# Revit family: Spout_Wall_Abey_Vela_165_FaceBased
name_source: partatom
category: Plumbing Fixtures
units: mm (PartAtom-declared; Revit-internal decimal feet)

## family parameters
Cut with Voids When Loaded = No
Host = Face
OmniClass Number = 23.31.11.00
OmniClass Title = Faucets
Part Type = Normal
Room Calculation Point = No
Round Connector Dimension = Use Diameter
Shared = No

## types (5) — shared parameters
Assembly Code = C1030210
CW Connection = Yes
Default Elevation = 0 mm
Description = Manufactured from low-lead brass, the Vela Bathroom Collection will transform your bathroom into a sanctuary of grace, serenity and purification.
HW Connection = Yes
IfcExportAs = ifcValve
IfcExportType = FAUCET
Manufacturer = Abey
ManufacturerOverallDepth = 182 mm
ManufacturerOverallHeight = 65 mm
ManufacturerOverallWidth = 65 mm
ManufacturerURLProductSpecific = https://www.abey.com.au
ModifiedIssue = 20230628 $
URL = https://www.abey.com.au
Uniclass2015Code = Pr_40_20_87_97
Uniclass2015Title = Washbasin spouts
Uniclass2015Version = Products v1.28
Vent Connection = No
Waste Connection = No
zero-valued in all types: Cost

## per-type parameters (varying)
| type | BodyMaterial | ManufacturerSpecCode | Model | Type Comments |
| Black (7S-C165-B) | Metal_Abey_Black | 7S-C165-B | 7S-C165-B | Black |
| Brushed Brass (7S-C165-BB) | Metal_Abey_Brass | 7S-C165-BB | 7S-C165-BB | Brushed Brass |
| Brushed Nickel (7S-C165-BN) | Metal_Abey_BrushedNickel | 7S-C165-BN | 7S-C165-BN | Brushed Nickel |
| Chrome (7S-C165) | Metal_Abey_Chrome | 7S-C165 | 7S-C165 | Chrome |
| Gun Metal (7S-C165-GM) | Metal_Abey_GunMetal | 7S-C165-GM | 7S-C165-GM | Gun Metal |

## geometry (parser evidence)
native form markers: Sweep x5
no freeform markers — native parametric forms only
